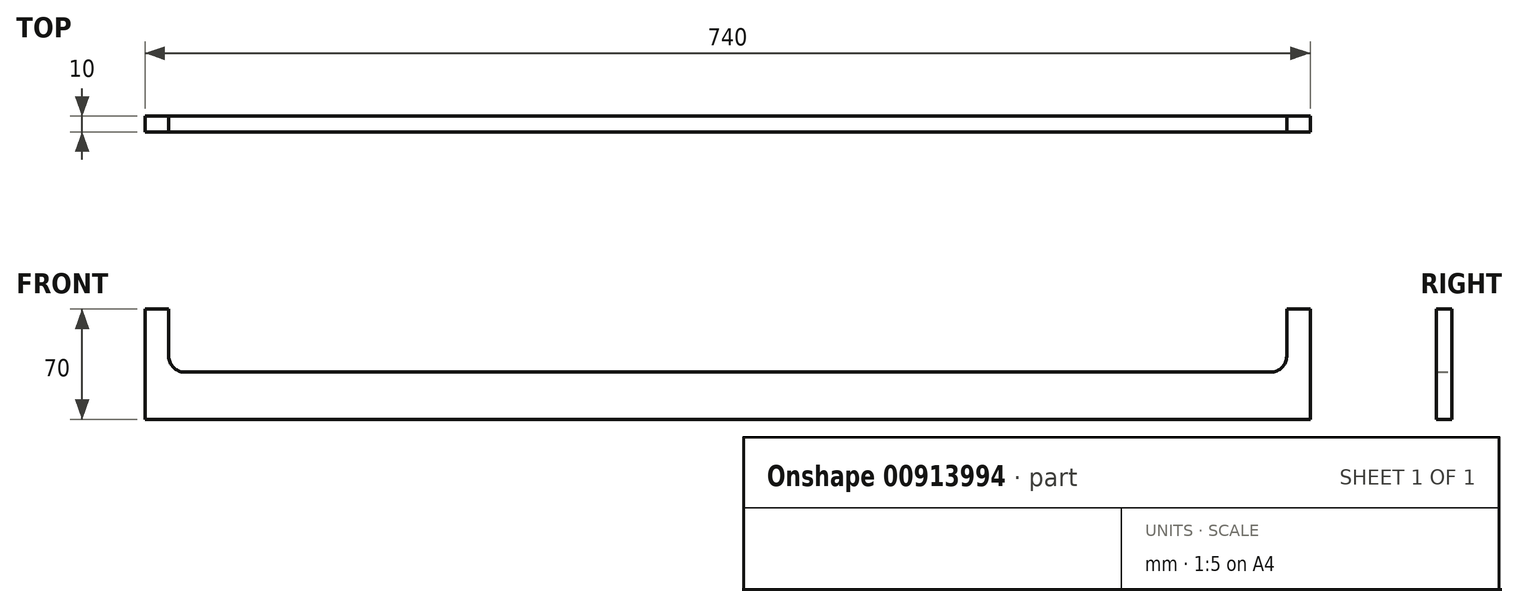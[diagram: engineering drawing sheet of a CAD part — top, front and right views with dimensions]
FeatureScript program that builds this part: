
annotation { "Feature Type Name" : "Feature", "Feature Type Description" : "" }
export const myFeature = defineFeature(function(context is Context, id is Id, definition is map)
    precondition{}
    {
        {
            var Q0;
            Q0=qCreatedBy(makeId("Front.planeOp"),FACE);
            var sketch = newSketch(context, id + "F0", { "sketchPlane" : qUnion([Q0])});
            skLineSegment(sketch, "E0", {"start": v(0, 0) * mm, "end": v(-345, 0) * mm});
            skArc(sketch, "E1", {"start": v(-345, 0) * mm, "mid": v(-352.07, 2.93) * mm, "end": v(-355, 10) * mm});
            skLineSegment(sketch, "E2", {"start": v(-355, 10) * mm, "end": v(-355, 40) * mm});
            skLineSegment(sketch, "E3", {"start": v(-355, 40) * mm, "end": v(-370, 40) * mm});
            skLineSegment(sketch, "E4", {"start": v(-370, 40) * mm, "end": v(-370, -30) * mm});
            skLineSegment(sketch, "E5", {"start": v(0, 0) * mm, "end": v(0, -30) * mm});
            skLineSegment(sketch, "E6", {"start": v(0, -30) * mm, "end": v(-370, -30) * mm});
            skSolve(sketch);
        }
        {
            var Q0;
            Q0 = qSketchRegion(id + "F0", true);
            extrude(context, id + "F1", {"entities" : qUnion([Q0]), "depth" : 10 * mm, "offsetDistance" : 25 * mm});
        }
        {
            var Q0;
            Q0=makeQuery(id+"F1.opExtrude","SWEPT_BODY",BODY,{"disambiguationData":[OSD([sQuery(id+"F0.wireOp",EDGE,"E0"),sQuery(id+"F0.wireOp",EDGE,"E1"),sQuery(id+"F0.wireOp",EDGE,"E2"),sQuery(id+"F0.wireOp",EDGE,"E3"),sQuery(id+"F0.wireOp",EDGE,"E4"),sQuery(id+"F0.wireOp",EDGE,"E5"),sQuery(id+"F0.wireOp",EDGE,"E6")])]});
            var Q1;
            Q1=makeQuery(id+"F1.opExtrude","SWEPT_FACE",FACE,{"disambiguationData":[OSD([sQuery(id+"F0.wireOp",EDGE,"E5")])]});
            mirror(context, id + "F2", {"operationType" : NewBodyOperationType.ADD, "entities" : qUnion([Q0]), "mirrorPlane" : qUnion([Q1])});
        }
    });
